# Revit family: Faucet_Single_Control-American_Standard-Towsend_7573.101
name_source: partatom
category: Plumbing Fixtures
revit_build: Autodesk Revit 2014 (Build: 20130308_1515(x64)
units: mm (PartAtom-declared; Revit-internal decimal feet)

## types (1)
- 7353.101
    ADA Compliant = Yes
    Assembly Code = D2020300
    CW Connection = Yes
    CWFU = 1.5
    Cold Water Connection Diameter = 0' - 0 3/8"
    Default Elevation = 0' - 0"
    Description = Townsend Single Control Lavatory Faucet
    HW Connection = Yes
    HWFU = 1.5
    Height = 0' - 7 13/16"
    Hot Water Connection Diameter = 0' - 0 3/8"
    Length = 0' - 7 1/4"
    Manufacturer = American Standard
    Material = Brass-American Standard-278-Legacy Bronze
    Model = 7353.101
    Product Documentation Link = https://www.americanstandard-us.com
    Product Page URL = https://www.americanstandard-us.com
    Revised Date = 05/11/2017
    Specification = Metal lever handle. Metal Speed Connect pop-up drain.
    URL = http://www.americanstandard-us.com
    Vent Connection = No
    WFU = 0
    Waste Connection = Yes
    Width = 0' - 2 1/4"

## geometry (parser evidence)
native form markers: Sweep x1
no freeform markers — native parametric forms only
